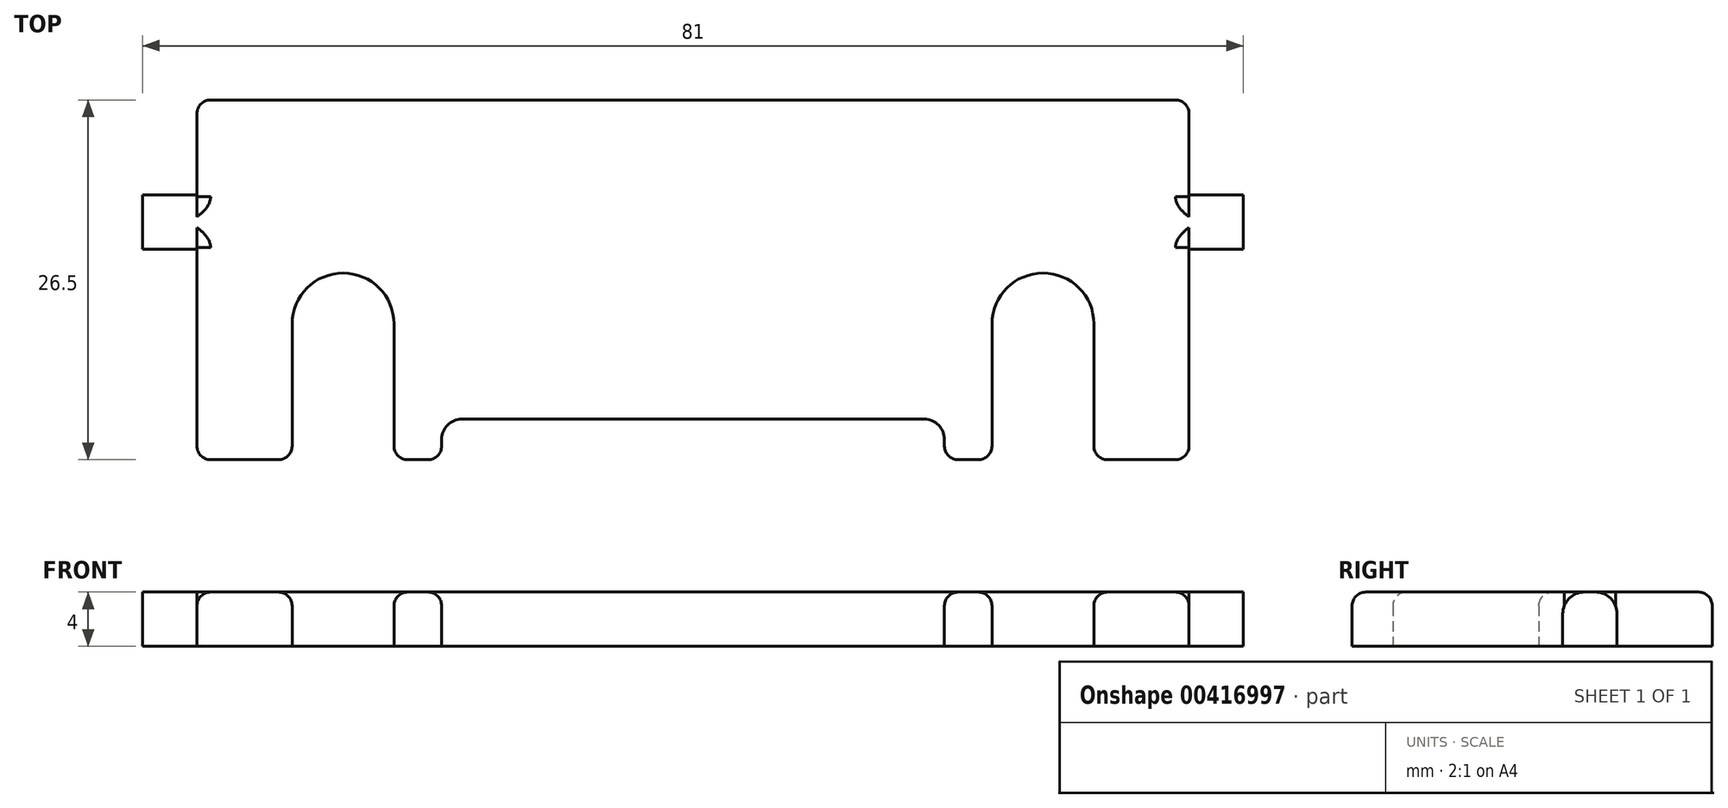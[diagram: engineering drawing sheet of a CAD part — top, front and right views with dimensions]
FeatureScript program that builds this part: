
annotation { "Feature Type Name" : "Feature", "Feature Type Description" : "" }
export const myFeature = defineFeature(function(context is Context, id is Id, definition is map)
    precondition{}
    {
        {
            var Q0;
            Q0=qCreatedBy(makeId("Top.planeOp"),FACE);
            var sketch = newSketch(context, id + "F0", { "sketchPlane" : qUnion([Q0])});
            skLineSegment(sketch, "E0.bottom", {"start": v(36.5, 13.25) * mm, "end": v(-36.5, 13.25) * mm});
            skLineSegment(sketch, "E0.top", {"start": v(36.5, -13.25) * mm, "end": v(-36.5, -13.25) * mm});
            skLineSegment(sketch, "E0.left", {"start": v(36.5, 13.25) * mm, "end": v(36.5, -13.25) * mm});
            skLineSegment(sketch, "E0.right", {"start": v(-36.5, 13.25) * mm, "end": v(-36.5, -13.25) * mm});
            skPoint(sketch, "E0.middle", {"position": v(0, 0) * mm});
            skLineSegment(sketch, "E1.bottom", {"start": v(-18.5, -13.25) * mm, "end": v(18.5, -13.25) * mm});
            skLineSegment(sketch, "E1.top", {"start": v(-18.5, -10.25) * mm, "end": v(18.5, -10.25) * mm});
            skLineSegment(sketch, "E1.left", {"start": v(-18.5, -13.25) * mm, "end": v(-18.5, -10.25) * mm});
            skLineSegment(sketch, "E1.right", {"start": v(18.5, -13.25) * mm, "end": v(18.5, -10.25) * mm});
            skLineSegment(sketch, "E2", {"start": v(22, -13.25) * mm, "end": v(22, -3.25) * mm});
            skLineSegment(sketch, "E3", {"start": v(29.5, -13.25) * mm, "end": v(29.5, -3.25) * mm});
            skLineSegment(sketch, "E4", {"start": v(29.5, -3.25) * mm, "end": v(22, -3.25) * mm, "construction": true});
            skArc(sketch, "E5", {"start": v(29.5, -3.25) * mm, "mid": v(25.75, 0.5) * mm, "end": v(22, -3.25) * mm});
            skLineSegment(sketch, "E6.MirrorCS", {"start": v(-22, -13.25) * mm, "end": v(-22, -3.25) * mm});
            skLineSegment(sketch, "E7.MirrorCS", {"start": v(-29.5, -13.25) * mm, "end": v(-29.5, -3.25) * mm});
            skArc(sketch, "E8.MirrorCS", {"start": v(-29.5, -3.25) * mm, "mid": v(-25.75, 0.5) * mm, "end": v(-22, -3.25) * mm});
            skLineSegment(sketch, "E9.bottom", {"start": v(36.5, 6.25) * mm, "end": v(40.5, 6.25) * mm});
            skLineSegment(sketch, "E9.top", {"start": v(36.5, 2.25) * mm, "end": v(40.5, 2.25) * mm});
            skLineSegment(sketch, "E9.left", {"start": v(36.5, 6.25) * mm, "end": v(36.5, 2.25) * mm});
            skLineSegment(sketch, "E9.right", {"start": v(40.5, 6.25) * mm, "end": v(40.5, 2.25) * mm});
            skLineSegment(sketch, "E10.MirrorCS", {"start": v(-36.5, 2.25) * mm, "end": v(-40.5, 2.25) * mm});
            skLineSegment(sketch, "E11.MirrorCS", {"start": v(-36.5, 6.25) * mm, "end": v(-40.5, 6.25) * mm});
            skLineSegment(sketch, "E12.MirrorCS", {"start": v(-40.5, 6.25) * mm, "end": v(-40.5, 2.25) * mm});
            skSolve(sketch);
        }
        {
            var Q0;
            {var subQ3=sQuery(id+"F0.wireOp",EDGE,"E0.bottom");Q0=makeQuery(id+"F0.imprint","IMPRINT",FACE,{"disambiguationData":[TD([[makeQuery(id+"F0.imprint","IMPRINT",EDGE,{"derivedFrom":subQ3}),1.0]])]});}
            var Q1;
            {var subQ0=sQuery(id+"F0.wireOp",EDGE,"E10.MirrorCS");Q1=makeQuery(id+"F0.imprint","IMPRINT",FACE,{"disambiguationData":[TD([[makeQuery(id+"F0.imprint","IMPRINT",EDGE,{"derivedFrom":subQ0}),-1.0]])]});}
            var Q2;
            Q2=makeQuery(id+"F0.imprint","IMPRINT",FACE,{"disambiguationData":[TD([[makeQuery(id+"F0.imprint","IMPRINT",EDGE,{"derivedFrom":sQuery(id+"F0.wireOp",EDGE,"E9.bottom")}),-1.0]])]});
            extrude(context, id + "F1", {"entities" : qUnion([Q0, Q1, Q2]), "depth" : 4 * mm, "offsetDistance" : 25 * mm});
        }
        {
            var Q0;
            Q0=makeQuery(id+"F1.opExtrude","CAP_EDGE",EDGE,{"disambiguationData":[OSD([sQuery(id+"F0.wireOp",EDGE,"E9.bottom")])],"isStart":false});
            var Q1;
            Q1=makeQuery(id+"F1.opExtrude","CAP_EDGE",EDGE,{"disambiguationData":[OSD([sQuery(id+"F0.wireOp",EDGE,"E9.top")])],"isStart":false});
            var Q2;
            Q2=makeQuery(id+"F1.opExtrude","CAP_EDGE",EDGE,{"disambiguationData":[OSD([sQuery(id+"F0.wireOp",EDGE,"E10.MirrorCS")])],"isStart":false});
            var Q3;
            Q3=makeQuery(id+"F1.opExtrude","CAP_EDGE",EDGE,{"disambiguationData":[OSD([sQuery(id+"F0.wireOp",EDGE,"E11.MirrorCS")])],"isStart":false});
            fillet(context, id + "F2", {"entities" : qUnion([Q0, Q1, Q2, Q3]), "radius" : 1.6 * mm, "tangentPropagation" : true, "allowEdgeOverflow" : false});
        }
        {
            var Q0;
            Q0=makeQuery(id+"F1.opExtrude","SWEPT_EDGE",EDGE,{"disambiguationData":[OSD([sQuery(id+"F0.wireOp",EDGE,"E1.top"),sQuery(id+"F0.wireOp",EDGE,"E1.left")])]});
            var Q1;
            Q1=makeQuery(id+"F1.opExtrude","SWEPT_EDGE",EDGE,{"disambiguationData":[OSD([sQuery(id+"F0.wireOp",EDGE,"E1.top"),sQuery(id+"F0.wireOp",EDGE,"E1.right")])]});
            fillet(context, id + "F3", {"entities" : qUnion([Q0, Q1]), "radius" : 1.5 * mm, "tangentPropagation" : true, "allowEdgeOverflow" : false});
        }
        {
            var Q0;
            Q0=makeQuery(id+"F1.opExtrude","SWEPT_EDGE",EDGE,{"disambiguationData":[OSD([sQuery(id+"F0.wireOp",EDGE,"E0.top"),sQuery(id+"F0.wireOp",EDGE,"E0.right")])]});
            var Q1;
            Q1=makeQuery(id+"F1.opExtrude","SWEPT_EDGE",EDGE,{"disambiguationData":[OSD([sQuery(id+"F0.wireOp",EDGE,"E0.top"),sQuery(id+"F0.wireOp",EDGE,"E7.MirrorCS")])]});
            var Q2;
            Q2=makeQuery(id+"F1.opExtrude","SWEPT_EDGE",EDGE,{"disambiguationData":[OSD([sQuery(id+"F0.wireOp",EDGE,"E0.top"),sQuery(id+"F0.wireOp",EDGE,"E6.MirrorCS")])]});
            var Q3;
            Q3=makeQuery(id+"F1.opExtrude","SWEPT_EDGE",EDGE,{"disambiguationData":[OSD([sQuery(id+"F0.wireOp",EDGE,"E0.top"),sQuery(id+"F0.wireOp",EDGE,"E1.bottom"),sQuery(id+"F0.wireOp",EDGE,"E1.left")])]});
            var Q4;
            Q4=makeQuery(id+"F1.opExtrude","SWEPT_EDGE",EDGE,{"disambiguationData":[OSD([sQuery(id+"F0.wireOp",EDGE,"E0.top"),sQuery(id+"F0.wireOp",EDGE,"E1.bottom"),sQuery(id+"F0.wireOp",EDGE,"E1.right")])]});
            var Q5;
            Q5=makeQuery(id+"F1.opExtrude","SWEPT_EDGE",EDGE,{"disambiguationData":[OSD([sQuery(id+"F0.wireOp",EDGE,"E0.top"),sQuery(id+"F0.wireOp",EDGE,"E2")])]});
            var Q6;
            Q6=makeQuery(id+"F1.opExtrude","SWEPT_EDGE",EDGE,{"disambiguationData":[OSD([sQuery(id+"F0.wireOp",EDGE,"E0.top"),sQuery(id+"F0.wireOp",EDGE,"E3")])]});
            var Q7;
            Q7=makeQuery(id+"F1.opExtrude","SWEPT_EDGE",EDGE,{"disambiguationData":[OSD([sQuery(id+"F0.wireOp",EDGE,"E0.top"),sQuery(id+"F0.wireOp",EDGE,"E0.left")])]});
            var Q8;
            Q8=makeQuery(id+"F1.opExtrude","SWEPT_EDGE",EDGE,{"disambiguationData":[OSD([sQuery(id+"F0.wireOp",EDGE,"E0.bottom"),sQuery(id+"F0.wireOp",EDGE,"E0.right")])]});
            var Q9;
            Q9=makeQuery(id+"F1.opExtrude","SWEPT_EDGE",EDGE,{"disambiguationData":[OSD([sQuery(id+"F0.wireOp",EDGE,"E0.bottom"),sQuery(id+"F0.wireOp",EDGE,"E0.left")])]});
            var Q10;
            {var subQ0=sQuery(id+"F0.wireOp",EDGE,"E0.left");Q10=makeQuery(id+"F1.opExtrude","CAP_EDGE",EDGE,{"disambiguationData":[OSD([subQ0]),TDD([makeQuery(id+"F0.imprint","IMPRINT",EDGE,{"disambiguationData":[TD([[makeQuery(id+"F0.imprint","INTERSECT",VERTEX,{"derivedFrom":[sQuery(id+"F0.wireOp",EDGE,"E0.top"),subQ0]}),1.0]])],"derivedFrom":subQ0})])],"isStart":false});}
            var Q11;
            Q11=makeQuery(id+"F1.opExtrude","CAP_EDGE",EDGE,{"disambiguationData":[OSD([sQuery(id+"F0.wireOp",EDGE,"E0.bottom")])],"isStart":false});
            var Q12;
            {var subQ0=sQuery(id+"F0.wireOp",EDGE,"E0.left");Q12=makeQuery(id+"F1.opExtrude","CAP_EDGE",EDGE,{"disambiguationData":[OSD([subQ0]),TDD([makeQuery(id+"F0.imprint","IMPRINT",EDGE,{"disambiguationData":[TD([[makeQuery(id+"F0.imprint","INTERSECT",VERTEX,{"derivedFrom":[sQuery(id+"F0.wireOp",EDGE,"E0.bottom"),subQ0]}),-1.0]])],"derivedFrom":subQ0})])],"isStart":false});}
            var Q13;
            {var subQ0=sQuery(id+"F0.wireOp",EDGE,"E0.right");Q13=makeQuery(id+"F1.opExtrude","CAP_EDGE",EDGE,{"disambiguationData":[OSD([subQ0]),TDD([makeQuery(id+"F0.imprint","IMPRINT",EDGE,{"disambiguationData":[TD([[makeQuery(id+"F0.imprint","INTERSECT",VERTEX,{"derivedFrom":[sQuery(id+"F0.wireOp",EDGE,"E0.bottom"),subQ0]}),-1.0]])],"derivedFrom":subQ0})])],"isStart":false});}
            var Q14;
            {var subQ0=sQuery(id+"F0.wireOp",EDGE,"E0.right");Q14=makeQuery(id+"F1.opExtrude","CAP_EDGE",EDGE,{"disambiguationData":[OSD([subQ0]),TDD([makeQuery(id+"F0.imprint","IMPRINT",EDGE,{"disambiguationData":[TD([[makeQuery(id+"F0.imprint","INTERSECT",VERTEX,{"derivedFrom":[sQuery(id+"F0.wireOp",EDGE,"E0.top"),subQ0]}),1.0]])],"derivedFrom":subQ0})])],"isStart":false});}
            var Q15;
            Q15=makeQuery(id+"F1.opExtrude","CAP_EDGE",EDGE,{"disambiguationData":[OSD([sQuery(id+"F0.wireOp",EDGE,"E6.MirrorCS")])],"isStart":false});
            var Q16;
            Q16=makeQuery(id+"F1.opExtrude","CAP_EDGE",EDGE,{"disambiguationData":[OSD([sQuery(id+"F0.wireOp",EDGE,"E2")])],"isStart":false});
            var Q17;
            Q17=makeQuery(id+"F1.opExtrude","CAP_EDGE",EDGE,{"disambiguationData":[OSD([sQuery(id+"F0.wireOp",EDGE,"E1.top")])],"isStart":false});
            var Q18;
            {var subQ0=sQuery(id+"F0.wireOp",EDGE,"E0.top");Q18=makeQuery(id+"F1.opExtrude","CAP_EDGE",EDGE,{"disambiguationData":[OSD([subQ0]),TDD([makeQuery(id+"F0.imprint","IMPRINT",EDGE,{"disambiguationData":[TD([[makeQuery(id+"F0.imprint","INTERSECT",VERTEX,{"derivedFrom":[subQ0,sQuery(id+"F0.wireOp",EDGE,"E0.right")]}),1.0]])],"derivedFrom":subQ0})])],"isStart":false});}
            var Q19;
            {var subQ0=sQuery(id+"F0.wireOp",EDGE,"E0.top");Q19=makeQuery(id+"F1.opExtrude","CAP_EDGE",EDGE,{"disambiguationData":[OSD([subQ0]),TDD([makeQuery(id+"F0.imprint","IMPRINT",EDGE,{"disambiguationData":[TD([[makeQuery(id+"F0.imprint","INTERSECT",VERTEX,{"derivedFrom":[subQ0,sQuery(id+"F0.wireOp",EDGE,"E0.left")]}),-1.0]])],"derivedFrom":subQ0})])],"isStart":false});}
            var Q20;
            {var subQ0=sQuery(id+"F0.wireOp",EDGE,"E0.top");Q20=makeQuery(id+"F1.opExtrude","CAP_EDGE",EDGE,{"disambiguationData":[OSD([subQ0]),TDD([makeQuery(id+"F0.imprint","IMPRINT",EDGE,{"disambiguationData":[TD([[makeQuery(id+"F0.imprint","INTERSECT",VERTEX,{"derivedFrom":[subQ0,sQuery(id+"F0.wireOp",EDGE,"E2")]}),-1.0]])],"derivedFrom":subQ0})])],"isStart":false});}
            var Q21;
            {var subQ0=sQuery(id+"F0.wireOp",EDGE,"E0.top");Q21=makeQuery(id+"F1.opExtrude","CAP_EDGE",EDGE,{"disambiguationData":[OSD([subQ0]),TDD([makeQuery(id+"F0.imprint","IMPRINT",EDGE,{"disambiguationData":[TD([[makeQuery(id+"F0.imprint","INTERSECT",VERTEX,{"derivedFrom":[subQ0,sQuery(id+"F0.wireOp",EDGE,"E6.MirrorCS")]}),1.0]])],"derivedFrom":subQ0})])],"isStart":false});}
            fillet(context, id + "F4", {"entities" : qUnion([Q0, Q1, Q2, Q3, Q4, Q5, Q6, Q7, Q8, Q9, Q10, Q11, Q12, Q13, Q14, Q15, Q16, Q17, Q18, Q19, Q20, Q21]), "radius" : 1 * mm, "tangentPropagation" : true, "allowEdgeOverflow" : false});
        }
    });
